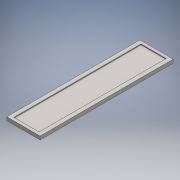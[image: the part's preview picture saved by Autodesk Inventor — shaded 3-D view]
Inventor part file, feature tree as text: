
AUTODESK INVENTOR PART (.ipt)
format: ipt  version: 2016 SP1 (Build 200210100, 210)  size: 119,296 bytes
history: native  units: mm
features: extrude x2, sketch x2
ambient origin geometry x8: Origin, YZ Plane, XZ Plane, XY Plane, X Axis, Y Axis, Z Axis, Center Point
bodies: Solid1 (feature_tree)
feature tree (4):
  extrude  "Extrusion1"  Depth=300.0mm
  extrude  "Extrusion2"  Depth=2.0mm
  sketch  "Sketch1"  dims[d0=75.0mm d1=300.0mm]
  sketch  "Sketch2"  dims[d2=150.0mm d3=37.5mm d4=8.0mm d5=0.0mm d6=57.0mm d7=287.0mm d8=143.5mm d9=28.5mm d10=2.0mm d11=0.0mm]
